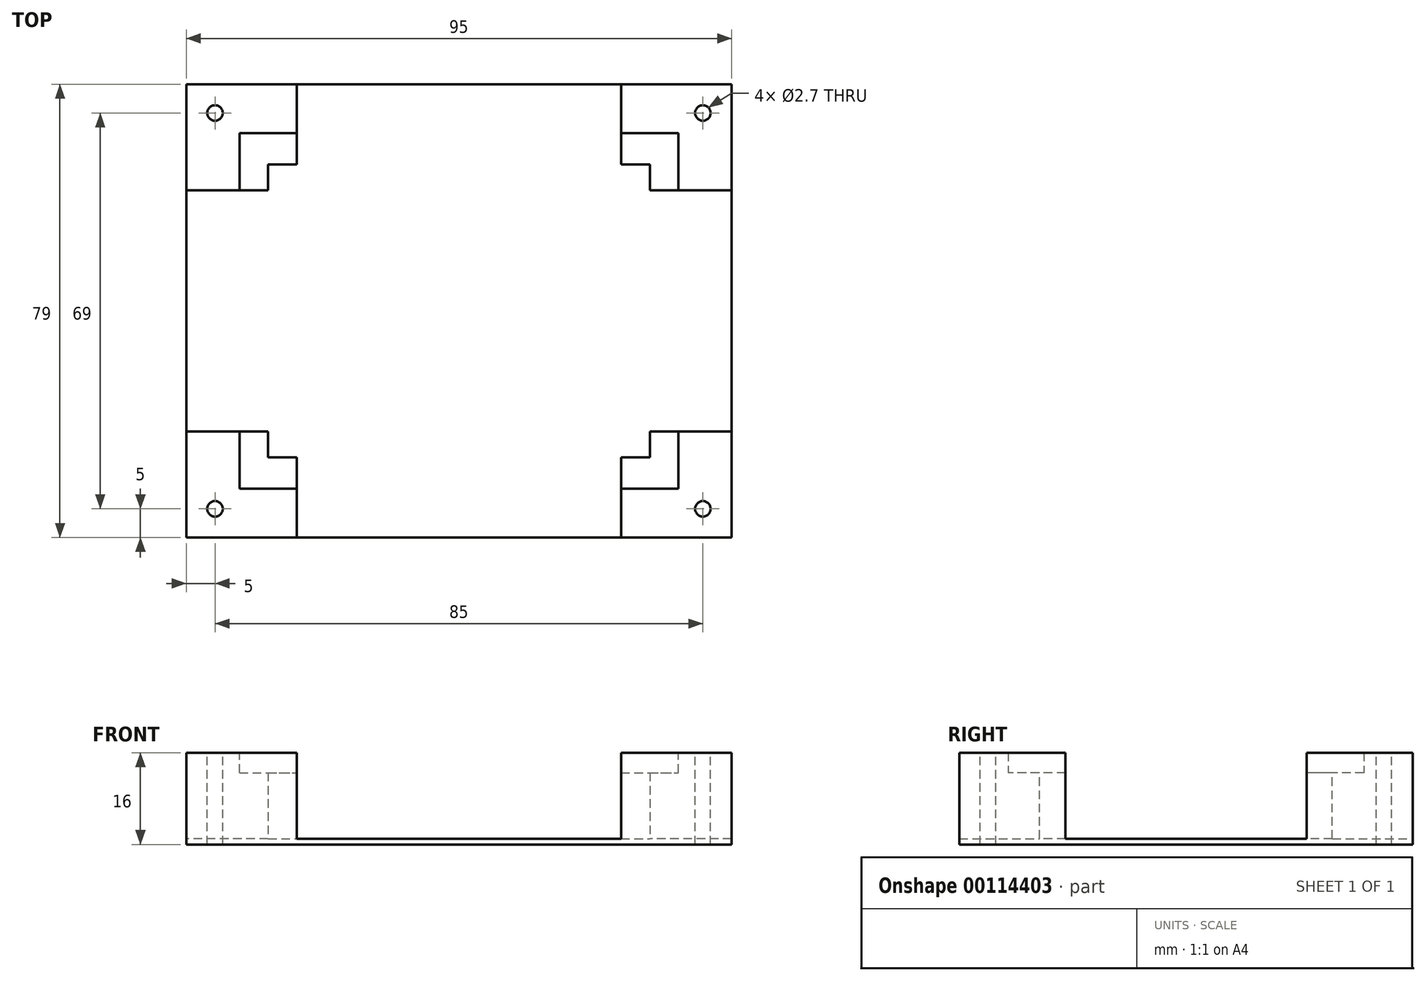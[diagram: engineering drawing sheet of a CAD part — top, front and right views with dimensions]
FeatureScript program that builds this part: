
annotation { "Feature Type Name" : "Feature", "Feature Type Description" : "" }
export const myFeature = defineFeature(function(context is Context, id is Id, definition is map)
    precondition{}
    {
        {
            var Q0;
            Q0=qCreatedBy(makeId("Top.planeOp"),FACE);
            var sketch = newSketch(context, id + "F0", { "sketchPlane" : qUnion([Q0])});
            skLineSegment(sketch, "E0.bottom", {"start": v(0, 0) * mm, "end": v(95, 0) * mm});
            skLineSegment(sketch, "E0.top", {"start": v(0, 79) * mm, "end": v(95, 79) * mm});
            skLineSegment(sketch, "E0.left", {"start": v(0, 0) * mm, "end": v(0, 79) * mm});
            skLineSegment(sketch, "E0.right", {"start": v(95, 0) * mm, "end": v(95, 79) * mm});
            skSolve(sketch);
        }
        {
            var Q0;
            Q0=makeQuery(id+"F0.imprint","IMPRINT",FACE,{"disambiguationData":[TD([[makeQuery(id+"F0.imprint","IMPRINT",EDGE,{"derivedFrom":sQuery(id+"F0.wireOp",EDGE,"E0.bottom")}),1.0]])]});
            extrude(context, id + "F1", {"entities" : qUnion([Q0]), "depth" : 1 * mm});
        }
        {
            var Q0;
            Q0=makeQuery(id+"F1.opExtrude","CAP_FACE",FACE,{"disambiguationData":[OSD([sQuery(id+"F0.wireOp",EDGE,"E0.bottom"),sQuery(id+"F0.wireOp",EDGE,"E0.top"),sQuery(id+"F0.wireOp",EDGE,"E0.left"),sQuery(id+"F0.wireOp",EDGE,"E0.right")])],"isStart":false});
            var sketch = newSketch(context, id + "F2", { "sketchPlane" : qUnion([Q0])});
            skLineSegment(sketch, "E1.0", {"start": v(0, 79) * mm, "end": v(95, 79) * mm});
            skLineSegment(sketch, "E1.1", {"start": v(0, 0) * mm, "end": v(0, 79) * mm});
            skLineSegment(sketch, "E1.2", {"start": v(0, 0) * mm, "end": v(95, 0) * mm});
            skLineSegment(sketch, "E1.3", {"start": v(95, 0) * mm, "end": v(95, 79) * mm});
            skLineSegment(sketch, "E2", {"start": v(47.5, 79) * mm, "end": v(47.5, 0) * mm, "construction": true});
            skLineSegment(sketch, "E3", {"start": v(95, 39.5) * mm, "end": v(0, 39.5) * mm, "construction": true});
            skLineSegment(sketch, "E4.bottom", {"start": v(14.25, 65) * mm, "end": v(80.75, 65) * mm});
            skLineSegment(sketch, "E4.top", {"start": v(14.25, 14) * mm, "end": v(80.75, 14) * mm});
            skLineSegment(sketch, "E4.left", {"start": v(14.25, 65) * mm, "end": v(14.25, 14) * mm});
            skLineSegment(sketch, "E4.right", {"start": v(80.75, 65) * mm, "end": v(80.75, 14) * mm});
            skPoint(sketch, "E5", {"position": v(14.25, 39.5) * mm});
            skPoint(sketch, "E6", {"position": v(47.5, 65) * mm});
            skSolve(sketch);
        }
        {
            var Q0;
            Q0=makeQuery(id+"F2.imprint","IMPRINT",FACE,{"disambiguationData":[TD([[makeQuery(id+"F2.imprint","IMPRINT",EDGE,{"derivedFrom":sQuery(id+"F2.wireOp",EDGE,"E1.0")}),-1.0]])]});
            extrude(context, id + "F3", {"entities" : qUnion([Q0]), "operationType" : NewBodyOperationType.ADD, "depth" : 15 * mm});
        }
        {
            var Q0;
            Q0=makeQuery(id+"F3.opExtrude","CAP_FACE",FACE,{"disambiguationData":[OSD([sQuery(id+"F2.wireOp",EDGE,"E1.0"),sQuery(id+"F2.wireOp",EDGE,"E1.1"),sQuery(id+"F2.wireOp",EDGE,"E1.2"),sQuery(id+"F2.wireOp",EDGE,"E1.3"),sQuery(id+"F2.wireOp",EDGE,"E4.bottom"),sQuery(id+"F2.wireOp",EDGE,"E4.top"),sQuery(id+"F2.wireOp",EDGE,"E4.left"),sQuery(id+"F2.wireOp",EDGE,"E4.right")])],"isStart":false});
            var sketch = newSketch(context, id + "F4", { "sketchPlane" : qUnion([Q0])});
            skLineSegment(sketch, "E7.0.0", {"start": v(0, 79) * mm, "end": v(0, 0) * mm});
            skLineSegment(sketch, "E7.0.1", {"start": v(0, 0) * mm, "end": v(95, 0) * mm});
            skLineSegment(sketch, "E7.0.2", {"start": v(95, 0) * mm, "end": v(95, 79) * mm});
            skLineSegment(sketch, "E7.0.3", {"start": v(95, 79) * mm, "end": v(0, 79) * mm});
            skLineSegment(sketch, "E8.1", {"start": v(14.25, 65) * mm, "end": v(14.25, 14) * mm});
            skLineSegment(sketch, "E9", {"start": v(0, 39.5) * mm, "end": v(95, 39.5) * mm, "construction": true});
            skLineSegment(sketch, "E10", {"start": v(47.5, 79) * mm, "end": v(47.5, 0) * mm, "construction": true});
            skLineSegment(sketch, "E11.bottom", {"start": v(9.25, 70.5) * mm, "end": v(85.75, 70.5) * mm});
            skLineSegment(sketch, "E11.top", {"start": v(9.25, 8.5) * mm, "end": v(85.75, 8.5) * mm});
            skLineSegment(sketch, "E11.left", {"start": v(9.25, 70.5) * mm, "end": v(9.25, 8.5) * mm});
            skLineSegment(sketch, "E11.right", {"start": v(85.75, 70.5) * mm, "end": v(85.75, 8.5) * mm});
            skPoint(sketch, "E12", {"position": v(47.5, 70.5) * mm});
            skPoint(sketch, "E13", {"position": v(9.25, 39.5) * mm});
            skSolve(sketch);
        }
        {
            var Q0;
            Q0=makeQuery(id+"F4.imprint","IMPRINT",FACE,{"disambiguationData":[TD([[makeQuery(id+"F4.imprint","IMPRINT",EDGE,{"derivedFrom":sQuery(id+"F4.wireOp",EDGE,"E8.1")}),-1.0]])]});
            extrude(context, id + "F5", {"entities" : qUnion([Q0]), "operationType" : NewBodyOperationType.REMOVE, "oppositeDirection" : true, "depth" : 3.5 * mm});
        }
        {
            var Q0;
            Q0=makeQuery(id+"F3.opExtrude","CAP_FACE",FACE,{"disambiguationData":[OSD([sQuery(id+"F2.wireOp",EDGE,"E1.0"),sQuery(id+"F2.wireOp",EDGE,"E1.1"),sQuery(id+"F2.wireOp",EDGE,"E1.2"),sQuery(id+"F2.wireOp",EDGE,"E1.3"),sQuery(id+"F2.wireOp",EDGE,"E4.bottom"),sQuery(id+"F2.wireOp",EDGE,"E4.top"),sQuery(id+"F2.wireOp",EDGE,"E4.left"),sQuery(id+"F2.wireOp",EDGE,"E4.right")])],"isStart":false});
            var sketch = newSketch(context, id + "F6", { "sketchPlane" : qUnion([Q0])});
            skLineSegment(sketch, "E14.bottom", {"start": v(0, 60.5) * mm, "end": v(95, 60.5) * mm});
            skLineSegment(sketch, "E14.top", {"start": v(0, 18.5) * mm, "end": v(95, 18.5) * mm});
            skLineSegment(sketch, "E14.left", {"start": v(0, 60.5) * mm, "end": v(0, 18.5) * mm});
            skLineSegment(sketch, "E14.right", {"start": v(95, 60.5) * mm, "end": v(95, 18.5) * mm});
            skLineSegment(sketch, "E15.bottom", {"start": v(19.25, 79) * mm, "end": v(75.75, 79) * mm});
            skLineSegment(sketch, "E15.top", {"start": v(19.25, 0) * mm, "end": v(75.75, 0) * mm});
            skLineSegment(sketch, "E15.left", {"start": v(19.25, 79) * mm, "end": v(19.25, 0) * mm});
            skLineSegment(sketch, "E15.right", {"start": v(75.75, 79) * mm, "end": v(75.75, 0) * mm});
            skSolve(sketch);
        }
        {
            var Q0;
            {var subQ0=sQuery(id+"F6.wireOp",EDGE,"E15.bottom");Q0=makeQuery(id+"F6.imprint","IMPRINT",FACE,{"disambiguationData":[TD([[makeQuery(id+"F6.imprint","IMPRINT",EDGE,{"derivedFrom":subQ0}),-1.0]])]});}
            var Q1;
            {var subQ0=sQuery(id+"F6.wireOp",EDGE,"E15.left");var subQ1=sQuery(id+"F6.wireOp",EDGE,"E14.bottom");var subQ2=makeQuery(id+"F6.imprint","INTERSECT",VERTEX,{"derivedFrom":[subQ1,subQ0]});Q1=makeQuery(id+"F6.imprint","IMPRINT",FACE,{"disambiguationData":[TD([[makeQuery(id+"F6.imprint","IMPRINT",EDGE,{"disambiguationData":[TD([[subQ2,-1.0]])],"derivedFrom":subQ1}),1.0]])]});}
            var Q2;
            {var subQ0=sQuery(id+"F6.wireOp",EDGE,"E15.left");var subQ1=sQuery(id+"F6.wireOp",EDGE,"E14.bottom");var subQ2=makeQuery(id+"F6.imprint","INTERSECT",VERTEX,{"derivedFrom":[subQ1,subQ0]});Q2=makeQuery(id+"F6.imprint","IMPRINT",FACE,{"disambiguationData":[TD([[makeQuery(id+"F6.imprint","IMPRINT",EDGE,{"disambiguationData":[TD([[subQ2,1.0]])],"derivedFrom":subQ1}),-1.0]])]});}
            var Q3;
            {var subQ0=sQuery(id+"F6.wireOp",EDGE,"E14.left");Q3=makeQuery(id+"F6.imprint","IMPRINT",FACE,{"disambiguationData":[TD([[makeQuery(id+"F6.imprint","IMPRINT",EDGE,{"derivedFrom":subQ0}),-1.0]])]});}
            var Q4;
            {var subQ0=sQuery(id+"F6.wireOp",EDGE,"E14.right");Q4=makeQuery(id+"F6.imprint","IMPRINT",FACE,{"disambiguationData":[TD([[makeQuery(id+"F6.imprint","IMPRINT",EDGE,{"derivedFrom":subQ0}),1.0]])]});}
            var Q5;
            {var subQ0=sQuery(id+"F6.wireOp",EDGE,"E15.right");var subQ1=sQuery(id+"F6.wireOp",EDGE,"E14.bottom");var subQ2=makeQuery(id+"F6.imprint","INTERSECT",VERTEX,{"derivedFrom":[subQ1,subQ0]});Q5=makeQuery(id+"F6.imprint","IMPRINT",FACE,{"disambiguationData":[TD([[makeQuery(id+"F6.imprint","IMPRINT",EDGE,{"disambiguationData":[TD([[subQ2,-1.0]])],"derivedFrom":subQ1}),-1.0]])]});}
            var Q6;
            {var subQ0=sQuery(id+"F6.wireOp",EDGE,"E15.top");Q6=makeQuery(id+"F6.imprint","IMPRINT",FACE,{"disambiguationData":[TD([[makeQuery(id+"F6.imprint","IMPRINT",EDGE,{"derivedFrom":subQ0}),1.0]])]});}
            var Q7;
            {var subQ0=sQuery(id+"F6.wireOp",EDGE,"E15.left");var subQ1=sQuery(id+"F6.wireOp",EDGE,"E14.top");var subQ2=makeQuery(id+"F6.imprint","INTERSECT",VERTEX,{"derivedFrom":[subQ1,subQ0]});Q7=makeQuery(id+"F6.imprint","IMPRINT",FACE,{"disambiguationData":[TD([[makeQuery(id+"F6.imprint","IMPRINT",EDGE,{"disambiguationData":[TD([[subQ2,-1.0]])],"derivedFrom":subQ1}),-1.0]])]});}
            var Q8;
            Q8=makeQuery(id+"F1.opExtrude","CAP_FACE",FACE,{"disambiguationData":[OSD([sQuery(id+"F0.wireOp",EDGE,"E0.bottom"),sQuery(id+"F0.wireOp",EDGE,"E0.top"),sQuery(id+"F0.wireOp",EDGE,"E0.left"),sQuery(id+"F0.wireOp",EDGE,"E0.right")])],"isStart":false});
            extrude(context, id + "F7", {"entities" : qUnion([Q0, Q1, Q2, Q3, Q4, Q5, Q6, Q7]), "operationType" : NewBodyOperationType.REMOVE, "endBound" : BoundingType.UP_TO_SURFACE, "oppositeDirection" : true, "endBoundEntityFace" : qUnion([Q8]), "depth" : 25 * mm});
        }
        {
            var Q0;
            {var subQ0=sQuery(id+"F2.wireOp",EDGE,"E1.1");var subQ1=sQuery(id+"F4.wireOp",EDGE,"E11.left");var subQ2=sQuery(id+"F2.wireOp",EDGE,"E1.0");var subQ4=sQuery(id+"F6.wireOp",EDGE,"E15.left");var subQ5=sQuery(id+"F6.wireOp",EDGE,"E14.bottom");var subQ6=makeQuery(id+"F6.imprint","INTERSECT",VERTEX,{"derivedFrom":[subQ5,subQ4]});var subQ8=makeQuery(id+"F6.imprint","INTERSECT",VERTEX,{"derivedFrom":[makeQuery(id+"F5.boolean.opBoolean","COPY",EDGE,{"derivedFrom":makeQuery(id+"F5.opExtrude","CAP_EDGE",EDGE,{"disambiguationData":[OSD([subQ1])],"isStart":true})}),subQ5]});Q0=makeQuery(id+"F7.boolean.opBoolean","SPLIT",FACE,{"disambiguationData":[TD([makeQuery(id+"F7.opExtrude","SWEPT_FACE",FACE,{"disambiguationData":[OSD([subQ5]),TDD([makeQuery(id+"F6.imprint","IMPRINT",EDGE,{"disambiguationData":[TD([[subQ8,1.0]])],"derivedFrom":subQ5}),makeQuery(id+"F6.imprint","IMPRINT",EDGE,{"disambiguationData":[TD([[subQ6,1.0]])],"derivedFrom":subQ5})])]})])],"derivedFrom":makeQuery(id+"F3.opExtrude","CAP_FACE",FACE,{"disambiguationData":[OSD([subQ2,subQ0,sQuery(id+"F2.wireOp",EDGE,"E1.2"),sQuery(id+"F2.wireOp",EDGE,"E1.3"),sQuery(id+"F2.wireOp",EDGE,"E4.bottom"),sQuery(id+"F2.wireOp",EDGE,"E4.top"),sQuery(id+"F2.wireOp",EDGE,"E4.left"),sQuery(id+"F2.wireOp",EDGE,"E4.right")])],"isStart":false})});}
            var sketch = newSketch(context, id + "F8", { "sketchPlane" : qUnion([Q0])});
            skLineSegment(sketch, "E16.bottom", {"start": v(5, 74) * mm, "end": v(90, 74) * mm, "construction": true});
            skLineSegment(sketch, "E16.top", {"start": v(5, 5) * mm, "end": v(90, 5) * mm, "construction": true});
            skLineSegment(sketch, "E16.left", {"start": v(5, 74) * mm, "end": v(5, 5) * mm, "construction": true});
            skLineSegment(sketch, "E16.right", {"start": v(90, 74) * mm, "end": v(90, 5) * mm, "construction": true});
            skCircle(sketch, "E17", {"center": v(5, 74) * mm, "radius": 1.35 * mm});
            skLineSegment(sketch, "E18.0", {"start": v(75.75, 79) * mm, "end": v(19.25, 79) * mm, "construction": true});
            skLineSegment(sketch, "E19", {"start": v(47.5, 79) * mm, "end": v(47.5, 0) * mm, "construction": true});
            skCircle(sketch, "E20", {"center": v(5, 5) * mm, "radius": 1.35 * mm});
            skCircle(sketch, "E21.MirrorC", {"center": v(90, 5) * mm, "radius": 1.35 * mm});
            skCircle(sketch, "E22.MirrorC", {"center": v(90, 74) * mm, "radius": 1.35 * mm});
            skSolve(sketch);
        }
        {
            var Q0;
            Q0 = qSketchRegion(id + "F8", true);
            extrude(context, id + "F9", {"entities" : qUnion([Q0]), "operationType" : NewBodyOperationType.REMOVE, "endBound" : BoundingType.THROUGH_ALL, "oppositeDirection" : true, "depth" : 25 * mm});
        }
    });
